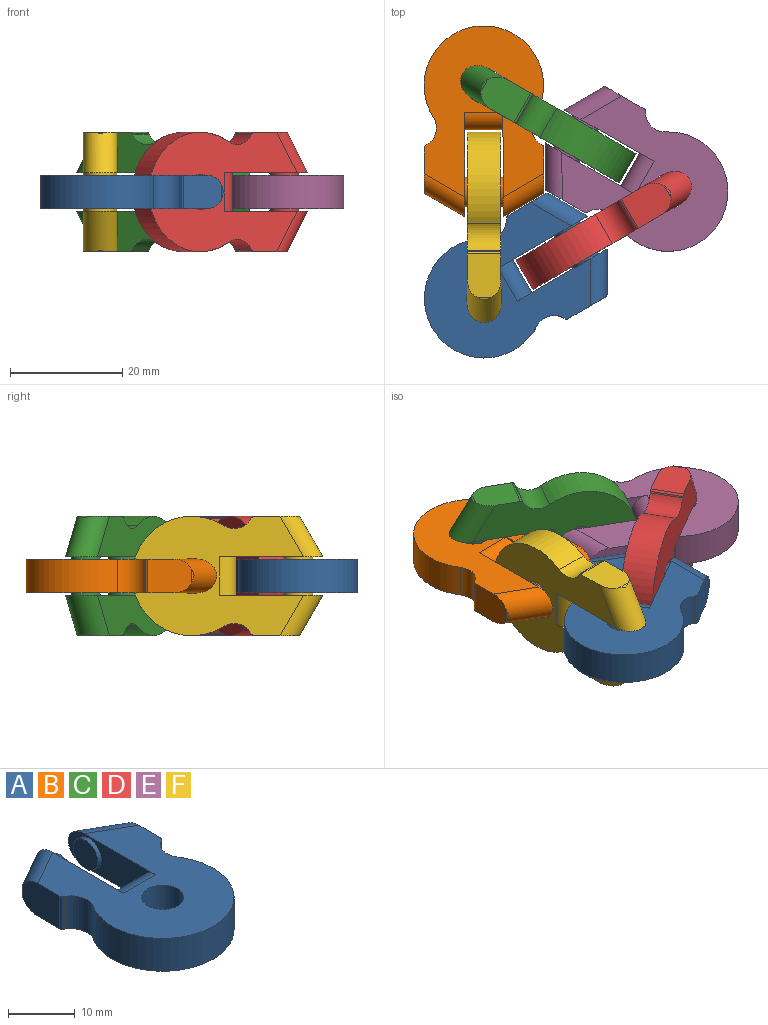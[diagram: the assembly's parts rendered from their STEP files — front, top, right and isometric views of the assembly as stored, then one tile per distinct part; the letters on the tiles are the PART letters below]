
ASSEMBLY  parts=6 mates=6
PART A: 23 faces, bbox 24.3x34x6 mm
  f0: plane 18.5x6mm, normal (-1,0,0), area 71.2mm2, adj f10,f11,f12,f18,f21
  f1: plane 18.5x6mm, normal (1,0,0), area 71.2mm2, adj f10,f11,f12,f17,f19
  f2: plane 7.79x6mm, normal (-1,0,0), area 43.6mm2, adj f10,f11,f13,f14,f17
  f3: plane 6x0.22mm, normal (-0.5,-0.87,0), area 1.5mm2, adj f4,f10,f11,f14
  f4: cylinder r=3.43mm len=6mm, axis (0,0,-1), area 33.2mm2, adj f3,f5,f10,f11
  f5: cylinder r=10.65mm len=21.3mm, axis (0,0,-1), area 272.9mm2, adj f4,f6,f10,f11
  f6: cylinder r=3.43mm len=6mm, axis (0,0,-1), area 33.2mm2, adj f5,f7,f10,f11
  f7: plane 6x0.22mm, normal (0.5,-0.87,0), area 1.5mm2, adj f6,f10,f11,f15
  f8: plane 7.79x6mm, normal (1,0,0), area 43.6mm2, adj f10,f11,f15,f16,f18
  f9: cylinder r=3.15mm len=6.3mm, axis (0,0,-1), area 118.8mm2, adj f10,f11
  f10: plane 30.53x21.3mm, normal (0,0,1), area 414.1mm2, adj f0,f1,f2,f3,f4,f5,f6,f7
  f11: plane 30.53x21.3mm, normal (0,0,-1), area 414.1mm2, adj f0,f1,f2,f3,f4,f5,f6,f7
  f12: cylinder r=3mm len=6.8mm, axis (1,0,0), area 64.1mm2, adj f0,f1,f10,f11
  f13: cylinder r=0.5mm len=2.4mm, axis (0,0,1), area 0.6mm2, adj f2,f17
  f14: cylinder r=0.5mm len=6mm, axis (0,0,1), area 3.1mm2, adj f2,f3,f10,f11
  f15: cylinder r=0.5mm len=6mm, axis (0,0,1), area 3.1mm2, adj f7,f8,f10,f11
  f16: cylinder r=0.5mm len=2.4mm, axis (0,0,1), area 0.6mm2, adj f8,f18
  f17: cylinder r=3mm len=10.26mm, axis (0.87,0.5,0), area 78.6mm2, adj f1,f2,f10,f11,f13
  f18: cylinder r=3mm len=10.26mm, axis (0.87,-0.5,0), area 78.6mm2, adj f0,f8,f10,f11,f16
  f19: cylinder r=2.6mm len=5.2mm, axis (-1,0,0), area 12.3mm2, adj f1,f20
  f20: plane 5.2x5.2mm, normal (1,0,0), area 21.2mm2, adj f19
  f21: cylinder r=2.6mm len=5.2mm, axis (1,0,0), area 12.3mm2, adj f0,f22
  f22: plane 5.2x5.2mm, normal (-1,0,0), area 21.2mm2, adj f21
PART B: same geometry as A
PART C: same geometry as A
PART D: same geometry as A
PART E: same geometry as A
PART F: same geometry as A
PLACE A rot(axis=(0.5,0.87,0),180deg) t=(18.14,-17.21,-4.96)mm
PLACE B rot(axis=(0,0,-1),179.9deg) t=(18.08,20.7,-4.96)mm
PLACE C rot(axis=(0.45,-0.77,0.45),104.5deg) t=(34.5,11.25,-4.96)mm
PLACE D rot(axis=(-0.45,-0.78,-0.45),104.4deg) t=(34.54,-7.7,-4.96)mm
PLACE E rot(axis=(0,0,1),60.1deg) t=(50.93,1.8,-4.96)mm fixed
PLACE F rot(axis=(0.71,0,-0.71),179.9deg) t=(18.11,1.75,-4.96)mm
MATE revolute D.f19 <-> E.f9  axis (0,0,1) through (50.93,1.8,-4.96)mm
MATE revolute F.f9 <-> B.f19  axis (1,0,0) through (18.11,1.75,-4.96)mm
MATE revolute F.f19 <-> A.f9  axis (0,0,-1) through (18.14,-17.21,-4.96)mm
MATE revolute C.f19 <-> B.f9  axis (0,0,1) through (18.08,20.7,-4.96)mm
MATE revolute D.f9 <-> A.f19  axis (0.5,-0.87,0) through (34.54,-7.7,-4.96)mm
MATE revolute C.f9 <-> E.f19  axis (0.5,0.87,0) through (34.5,11.25,-4.96)mm
